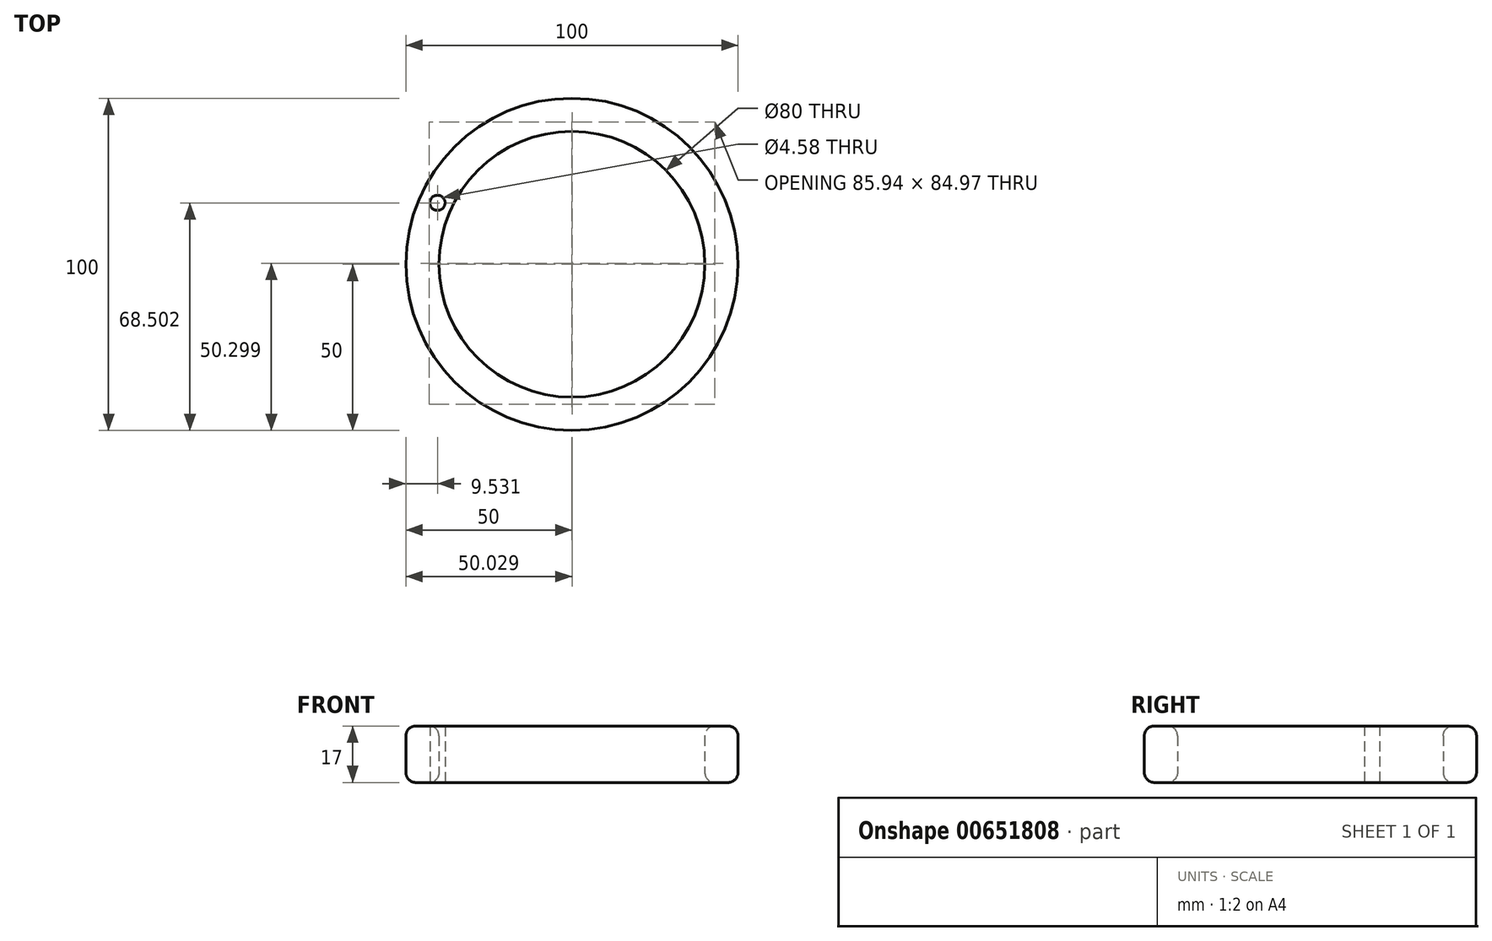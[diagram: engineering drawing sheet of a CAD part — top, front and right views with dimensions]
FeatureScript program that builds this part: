
annotation { "Feature Type Name" : "Feature", "Feature Type Description" : "" }
export const myFeature = defineFeature(function(context is Context, id is Id, definition is map)
    precondition{}
    {
        {
            var Q0;
            Q0=qCreatedBy(makeId("Top.planeOp"),FACE);
            var sketch = newSketch(context, id + "F0", { "sketchPlane" : qUnion([Q0])});
            skCircle(sketch, "E0", {"center": v(0, 0) * mm, "radius": 50 * mm});
            skCircle(sketch, "E1", {"center": v(0, 0) * mm, "radius": 40 * mm});
            skCircle(sketch, "E2", {"center": v(-40.47, 18.5) * mm, "radius": 2.3 * mm});
            skSolve(sketch);
        }
        {
            var Q0;
            Q0 = qSketchRegion(id + "F0", true);
            extrude(context, id + "F1", {"entities" : qUnion([Q0]), "depth" : 17 * mm, "offsetDistance" : 25 * mm});
        }
        {
            var Q0;
            Q0=makeQuery(id+"F1.opExtrude","SWEPT_FACE",FACE,{"disambiguationData":[OSD([sQuery(id+"F0.wireOp",EDGE,"E0")])]});
            var Q1;
            Q1=makeQuery(id+"F1.opExtrude","CAP_EDGE",EDGE,{"disambiguationData":[OSD([sQuery(id+"F0.wireOp",EDGE,"E1")])],"isStart":false});
            var Q2;
            Q2=makeQuery(id+"F1.opExtrude","CAP_EDGE",EDGE,{"disambiguationData":[OSD([sQuery(id+"F0.wireOp",EDGE,"E1")])],"isStart":true});
            fillet(context, id + "F2", {"entities" : qUnion([Q0, Q1, Q2]), "radius" : 3 * mm, "tangentPropagation" : true, "allowEdgeOverflow" : false});
        }
    });
